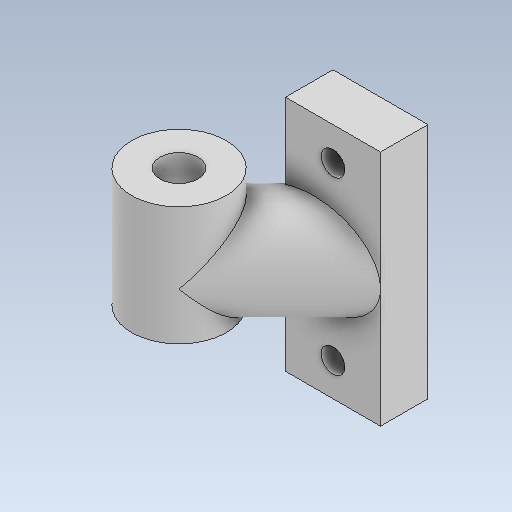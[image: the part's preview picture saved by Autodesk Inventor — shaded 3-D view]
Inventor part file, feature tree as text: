
AUTODESK INVENTOR PART (.ipt)
format: ipt  version: 2020 (Build 240168000, 168)  size: 168,960 bytes
history: native  units: mm
features: extrude x4, sketch x4, plane x2, projected_geometry x2, split x1
ambient origin geometry x8: Origin, YZ Plane, XZ Plane, XY Plane, X Axis, Y Axis, Z Axis, Center Point
bodies: Solid1 (feature_tree)
feature tree (13):
  extrude  "Extrusion1"  Depth=50.0mm
  plane  "Work Plane1"
  plane  "Work Plane2"
  extrude  "Extrusion6"  Depth=7.0mm
  split  "Split1"
  extrude  "Extrusion7"  Depth=10.0mm TaperAngle=0.0deg
  extrude  "Extrusion8"  [1 undecoded]
  sketch  "Sketch1"  dims[d0=20.0mm d1=50.0mm]
  sketch  "Sketch7"  dims[d2=5.0mm d3=7.0mm]
  sketch  "Sketch8"  dims[d4=7.0mm d5=10.0mm d6=0.0mm]
  sketch  "Sketch9"  dims[d11=-10.0mm d27=-7.853982mm d28=20.0mm d29=10.0mm d30=30.0mm d31=0.0mm d32=20.0mm d33=25.0mm d34=0.0mm d35=8.0mm d36=30.0mm d37=0.0mm]
  projected_geometry  "Project Cut Edges2"
  projected_geometry  "Project Cut Edges3"
note: 1 required parameter value undecoded (feature->parameter linkage not recoverable at this tier; creation-order binding heuristic only, values carry confidence <= 0.55)
